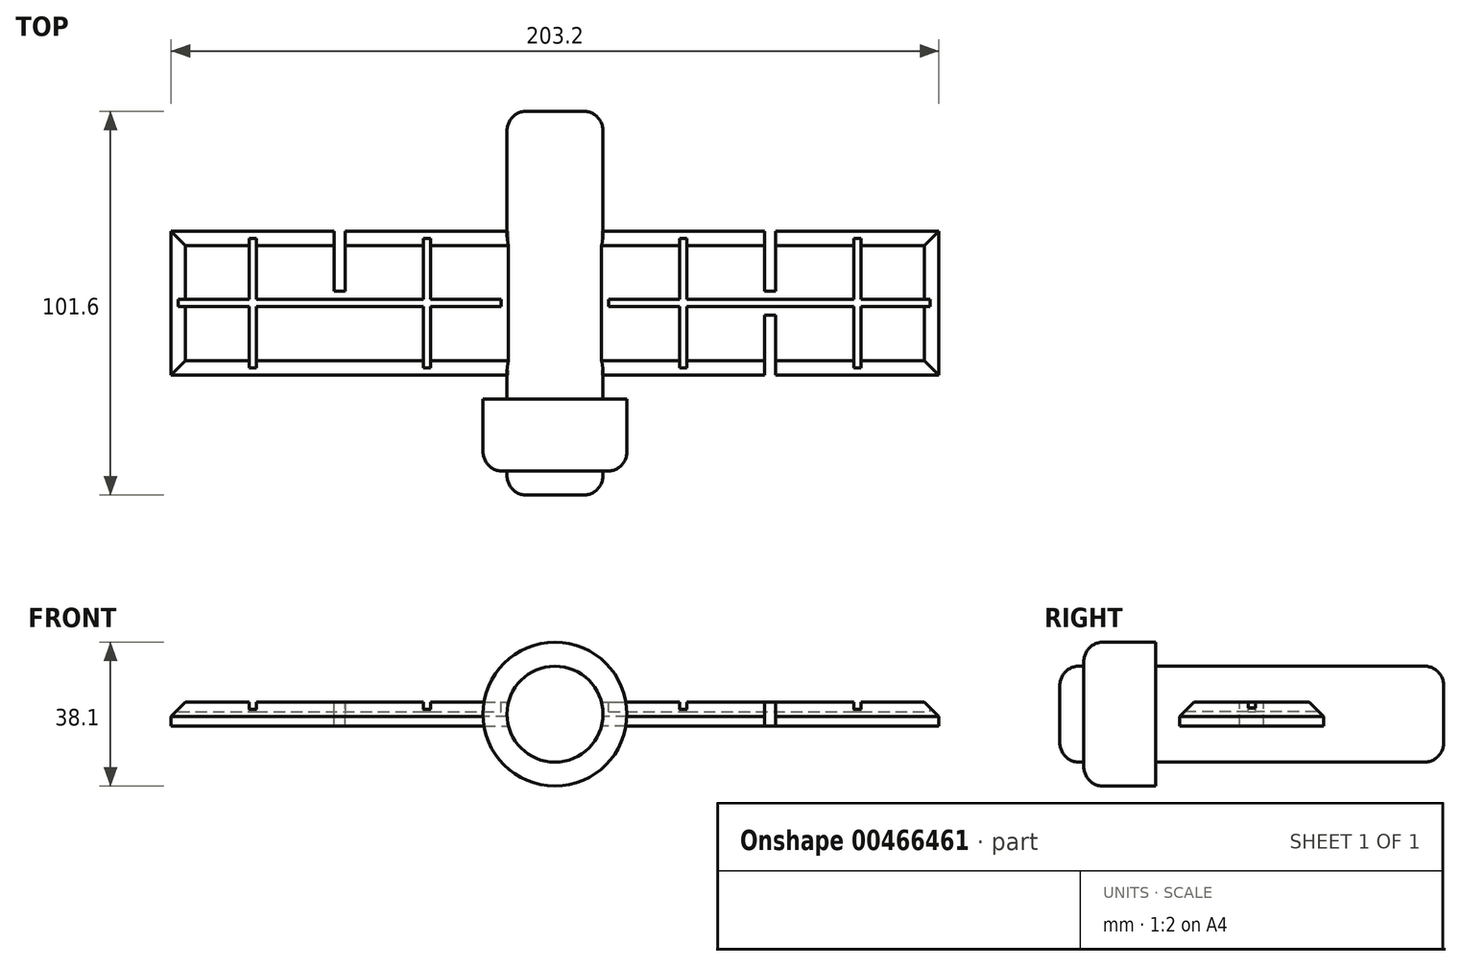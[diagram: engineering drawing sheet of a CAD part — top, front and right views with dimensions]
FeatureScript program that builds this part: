
annotation { "Feature Type Name" : "Feature", "Feature Type Description" : "" }
export const myFeature = defineFeature(function(context is Context, id is Id, definition is map)
    precondition{}
    {
        {
            var Q0;
            Q0=qCreatedBy(makeId("Front.planeOp"),FACE);
            cPlane(context, id + "F0", {"entities" : qUnion([Q0]), "cplaneType" : CPlaneType.OFFSET, "offset" : 50.8 * mm, "width" : 152.4 * mm, "height" : 152.4 * mm});
        }
        {
            var Q0;
            Q0=qCreatedBy(id+"F0.planeOp",FACE);
            var sketch = newSketch(context, id + "F1", { "sketchPlane" : qUnion([Q0])});
            skCircle(sketch, "E0", {"center": v(0, 0) * mm, "radius": 12.7 * mm});
            skSolve(sketch);
        }
        {
            var Q0;
            Q0=makeQuery(id+"F1.imprint","IMPRINT",FACE,{"disambiguationData":[TD([[makeQuery(id+"F1.imprint","IMPRINT",EDGE,{"derivedFrom":sQuery(id+"F1.wireOp",EDGE,"E0")}),1.0]])]});
            extrude(context, id + "F2", {"entities" : qUnion([Q0]), "oppositeDirection" : true, "depth" : 101.6 * mm});
        }
        {
            var Q0;
            Q0=makeQuery(id+"F2.opExtrude","CAP_EDGE",EDGE,{"disambiguationData":[OSD([sQuery(id+"F1.wireOp",EDGE,"E0")])],"isStart":true});
            var Q1;
            Q1=makeQuery(id+"F2.opExtrude","CAP_EDGE",EDGE,{"disambiguationData":[OSD([sQuery(id+"F1.wireOp",EDGE,"E0")])],"isStart":false});
            fillet(context, id + "F3", {"entities" : qUnion([Q0, Q1]), "radius" : 5.08 * mm, "tangentPropagation" : true, "allowEdgeOverflow" : false});
        }
        {
            var Q0;
            Q0=qCreatedBy(makeId("Right.planeOp"),FACE);
            var sketch = newSketch(context, id + "F4", { "sketchPlane" : qUnion([Q0])});
            skLineSegment(sketch, "E1.bottom", {"start": v(19.05, 3.17) * mm, "end": v(-19.05, 3.17) * mm});
            skLineSegment(sketch, "E1.top", {"start": v(19.05, -3.18) * mm, "end": v(-19.05, -3.18) * mm});
            skLineSegment(sketch, "E1.left", {"start": v(19.05, 3.17) * mm, "end": v(19.05, -3.18) * mm});
            skLineSegment(sketch, "E1.right", {"start": v(-19.05, 3.17) * mm, "end": v(-19.05, -3.18) * mm});
            skPoint(sketch, "E1.middle", {"position": v(0, 0) * mm});
            skSolve(sketch);
        }
        {
            var Q0;
            Q0 = qSketchRegion(id + "F4", true);
            extrude(context, id + "F5", {"entities" : qUnion([Q0]), "operationType" : NewBodyOperationType.ADD, "depth" : 101.6 * mm});
        }
        {
            var Q0;
            Q0 = qSketchRegion(id + "F4", true);
            extrude(context, id + "F6", {"entities" : qUnion([Q0]), "operationType" : NewBodyOperationType.ADD, "oppositeDirection" : true, "depth" : 101.6 * mm});
        }
        {
            var Q0;
            Q0=makeQuery(id+"F6.opExtrude","SWEPT_FACE",FACE,{"disambiguationData":[OSD([sQuery(id+"F4.wireOp",EDGE,"E1.bottom")])]});
            var sketch = newSketch(context, id + "F7", { "sketchPlane" : qUnion([Q0])});
            skLineSegment(sketch, "E2.bottom", {"start": v(-101.6, 19.05) * mm, "end": v(-58.42, 19.05) * mm, "construction": true});
            skLineSegment(sketch, "E2.top", {"start": v(-101.6, -19.05) * mm, "end": v(-58.42, -19.05) * mm, "construction": true});
            skLineSegment(sketch, "E2.left", {"start": v(-101.6, 19.05) * mm, "end": v(-101.6, -19.05) * mm, "construction": true});
            skLineSegment(sketch, "E2.right", {"start": v(-58.42, 19.05) * mm, "end": v(-58.42, -19.05) * mm, "construction": true});
            skLineSegment(sketch, "E3.bottom", {"start": v(-12.3, -19.05) * mm, "end": v(-55.48, -19.05) * mm, "construction": true});
            skLineSegment(sketch, "E3.top", {"start": v(-12.3, 19.05) * mm, "end": v(-55.48, 19.05) * mm, "construction": true});
            skLineSegment(sketch, "E3.left", {"start": v(-12.3, -19.05) * mm, "end": v(-12.3, 19.05) * mm, "construction": true});
            skLineSegment(sketch, "E3.right", {"start": v(-55.48, -19.05) * mm, "end": v(-55.48, 19.05) * mm, "construction": true});
            skLineSegment(sketch, "E4", {"start": v(-58.42, 0) * mm, "end": v(-55.48, 0) * mm, "construction": true});
            skLineSegment(sketch, "E5.top", {"start": v(-58.42, 3.18) * mm, "end": v(-55.48, 3.18) * mm, "construction": true});
            skLineSegment(sketch, "E5.left", {"start": v(-58.42, 0) * mm, "end": v(-58.42, 3.18) * mm, "construction": true});
            skLineSegment(sketch, "E5.right", {"start": v(-55.48, 0) * mm, "end": v(-55.48, 3.18) * mm, "construction": true});
            skLineSegment(sketch, "E6.bottom", {"start": v(-58.42, 0) * mm, "end": v(-55.48, 0) * mm});
            skLineSegment(sketch, "E6.top", {"start": v(-58.42, -3.17) * mm, "end": v(-55.48, -3.17) * mm});
            skLineSegment(sketch, "E6.left", {"start": v(-58.42, 0) * mm, "end": v(-58.42, -3.17) * mm});
            skLineSegment(sketch, "E6.right", {"start": v(-55.48, 0) * mm, "end": v(-55.48, -3.17) * mm});
            skLineSegment(sketch, "E7.top", {"start": v(-58.42, -19.05) * mm, "end": v(-55.48, -19.05) * mm});
            skLineSegment(sketch, "E7.left", {"start": v(-58.42, -3.17) * mm, "end": v(-58.42, -19.05) * mm});
            skLineSegment(sketch, "E7.right", {"start": v(-55.48, -3.17) * mm, "end": v(-55.48, -19.05) * mm});
            skLineSegment(sketch, "E8.bottom", {"start": v(-58.42, 19.05) * mm, "end": v(-55.48, 19.05) * mm});
            skLineSegment(sketch, "E8.top", {"start": v(-58.42, 3.18) * mm, "end": v(-55.48, 3.18) * mm});
            skLineSegment(sketch, "E8.left", {"start": v(-58.42, 19.05) * mm, "end": v(-58.42, 3.18) * mm});
            skLineSegment(sketch, "E8.right", {"start": v(-55.48, 19.05) * mm, "end": v(-55.48, 3.18) * mm});
            skSolve(sketch);
        }
        {
            var Q0;
            Q0=makeQuery(id+"F7.imprint","IMPRINT",FACE,{"disambiguationData":[TD([[makeQuery(id+"F7.imprint","IMPRINT",EDGE,{"derivedFrom":sQuery(id+"F7.wireOp",EDGE,"E8.bottom")}),-1.0]])]});
            var Q1;
            Q1=makeQuery(id+"F7.imprint","IMPRINT",FACE,{"disambiguationData":[TD([[makeQuery(id+"F7.imprint","IMPRINT",EDGE,{"derivedFrom":sQuery(id+"F7.wireOp",EDGE,"E6.top")}),-1.0]])]});
            extrude(context, id + "F8", {"entities" : qUnion([Q0, Q1]), "operationType" : NewBodyOperationType.REMOVE, "oppositeDirection" : true, "depth" : 25.4 * mm});
        }
        {
            var Q0;
            Q0=makeQuery(id+"F5.opExtrude","SWEPT_FACE",FACE,{"disambiguationData":[OSD([sQuery(id+"F4.wireOp",EDGE,"E1.bottom")])]});
            var sketch = newSketch(context, id + "F9", { "sketchPlane" : qUnion([Q0])});
            skLineSegment(sketch, "E9.bottom", {"start": v(12.3, 19.05) * mm, "end": v(55.48, 19.05) * mm, "construction": true});
            skLineSegment(sketch, "E9.top", {"start": v(12.3, -19.05) * mm, "end": v(55.48, -19.05) * mm, "construction": true});
            skLineSegment(sketch, "E9.left", {"start": v(12.3, 19.05) * mm, "end": v(12.3, -19.05) * mm, "construction": true});
            skLineSegment(sketch, "E9.right", {"start": v(55.48, 19.05) * mm, "end": v(55.48, -19.05) * mm, "construction": true});
            skLineSegment(sketch, "E10.bottom", {"start": v(101.6, -19.05) * mm, "end": v(58.42, -19.05) * mm, "construction": true});
            skLineSegment(sketch, "E10.top", {"start": v(101.6, 19.05) * mm, "end": v(58.42, 19.05) * mm, "construction": true});
            skLineSegment(sketch, "E10.left", {"start": v(101.6, -19.05) * mm, "end": v(101.6, 19.05) * mm, "construction": true});
            skLineSegment(sketch, "E10.right", {"start": v(58.42, -19.05) * mm, "end": v(58.42, 19.05) * mm, "construction": true});
            skLineSegment(sketch, "E11", {"start": v(55.48, 0) * mm, "end": v(58.42, 0) * mm, "construction": true});
            skLineSegment(sketch, "E12.top", {"start": v(55.48, 3.18) * mm, "end": v(58.42, 3.18) * mm, "construction": true});
            skLineSegment(sketch, "E12.left", {"start": v(55.48, 0) * mm, "end": v(55.48, 3.18) * mm, "construction": true});
            skLineSegment(sketch, "E12.right", {"start": v(58.42, 0) * mm, "end": v(58.42, 3.18) * mm, "construction": true});
            skLineSegment(sketch, "E13.top", {"start": v(55.48, -3.17) * mm, "end": v(58.42, -3.17) * mm, "construction": true});
            skLineSegment(sketch, "E13.left", {"start": v(55.48, 0) * mm, "end": v(55.48, -3.17) * mm, "construction": true});
            skLineSegment(sketch, "E13.right", {"start": v(58.42, 0) * mm, "end": v(58.42, -3.17) * mm, "construction": true});
            skLineSegment(sketch, "E14.bottom", {"start": v(55.48, -3.17) * mm, "end": v(58.42, -3.17) * mm});
            skLineSegment(sketch, "E14.top", {"start": v(55.48, -19.05) * mm, "end": v(58.42, -19.05) * mm});
            skLineSegment(sketch, "E14.left", {"start": v(55.48, -3.17) * mm, "end": v(55.48, -19.05) * mm});
            skLineSegment(sketch, "E14.right", {"start": v(58.42, -3.17) * mm, "end": v(58.42, -19.05) * mm});
            skLineSegment(sketch, "E15.bottom", {"start": v(55.48, 19.05) * mm, "end": v(58.42, 19.05) * mm});
            skLineSegment(sketch, "E15.top", {"start": v(55.48, 3.18) * mm, "end": v(58.42, 3.18) * mm});
            skLineSegment(sketch, "E15.left", {"start": v(55.48, 19.05) * mm, "end": v(55.48, 3.18) * mm});
            skLineSegment(sketch, "E15.right", {"start": v(58.42, 19.05) * mm, "end": v(58.42, 3.18) * mm});
            skSolve(sketch);
        }
        {
            var Q0;
            Q0=makeQuery(id+"F9.imprint","IMPRINT",FACE,{"disambiguationData":[TD([[makeQuery(id+"F9.imprint","IMPRINT",EDGE,{"derivedFrom":sQuery(id+"F9.wireOp",EDGE,"E15.bottom")}),1.0]])]});
            var Q1;
            Q1=makeQuery(id+"F9.imprint","IMPRINT",FACE,{"disambiguationData":[TD([[makeQuery(id+"F9.imprint","IMPRINT",EDGE,{"derivedFrom":sQuery(id+"F9.wireOp",EDGE,"E14.bottom")}),-1.0]])]});
            extrude(context, id + "F10", {"entities" : qUnion([Q0, Q1]), "operationType" : NewBodyOperationType.REMOVE, "oppositeDirection" : true, "depth" : 25.4 * mm});
        }
        {
            var Q0;
            Q0=makeQuery(id+"F6.opExtrude","SWEPT_FACE",FACE,{"disambiguationData":[OSD([sQuery(id+"F4.wireOp",EDGE,"E1.bottom")])]});
            var sketch = newSketch(context, id + "F11", { "sketchPlane" : qUnion([Q0])});
            skLineSegment(sketch, "E16.bottom", {"start": v(-79.06, 19.05) * mm, "end": v(-80.96, 19.05) * mm, "construction": true});
            skLineSegment(sketch, "E16.top", {"start": v(-79.06, 19.05) * mm, "end": v(-80.96, 19.05) * mm, "construction": true});
            skLineSegment(sketch, "E16.left", {"start": v(-79.06, 19.05) * mm, "end": v(-79.06, 19.05) * mm});
            skLineSegment(sketch, "E16.right", {"start": v(-80.96, 19.05) * mm, "end": v(-80.96, 19.05) * mm});
            skPoint(sketch, "E16.middle", {"position": v(-80.01, 19.05) * mm});
            skLineSegment(sketch, "E17", {"start": v(-80.96, 19.05) * mm, "end": v(-80.96, 17.15) * mm, "construction": true});
            skLineSegment(sketch, "E18.bottom", {"start": v(-80.96, 17.15) * mm, "end": v(-79.06, 17.15) * mm});
            skLineSegment(sketch, "E18.top", {"start": v(-80.96, -17.14) * mm, "end": v(-79.06, -17.14) * mm});
            skLineSegment(sketch, "E18.left", {"start": v(-80.96, 17.15) * mm, "end": v(-80.96, -17.14) * mm});
            skLineSegment(sketch, "E18.right", {"start": v(-79.06, 17.15) * mm, "end": v(-79.06, -17.14) * mm});
            skLineSegment(sketch, "E19.bottom", {"start": v(-101.6, 0.95) * mm, "end": v(-101.6, 0.95) * mm});
            skLineSegment(sketch, "E19.top", {"start": v(-101.6, -0.95) * mm, "end": v(-101.6, -0.95) * mm});
            skLineSegment(sketch, "E19.left", {"start": v(-101.6, 0.95) * mm, "end": v(-101.6, -0.95) * mm, "construction": true});
            skLineSegment(sketch, "E19.right", {"start": v(-101.6, 0.95) * mm, "end": v(-101.6, -0.95) * mm, "construction": true});
            skPoint(sketch, "E19.middle", {"position": v(-101.6, 0) * mm});
            skLineSegment(sketch, "E20.bottom", {"start": v(-101.6, -0.95) * mm, "end": v(-99.7, -0.95) * mm, "construction": true});
            skLineSegment(sketch, "E20.top", {"start": v(-101.6, 0.95) * mm, "end": v(-99.7, 0.95) * mm, "construction": true});
            skLineSegment(sketch, "E20.left", {"start": v(-101.6, -0.95) * mm, "end": v(-101.6, 0.95) * mm, "construction": true});
            skLineSegment(sketch, "E20.right", {"start": v(-99.7, -0.95) * mm, "end": v(-99.7, 0.95) * mm, "construction": true});
            skLineSegment(sketch, "E21.bottom", {"start": v(-99.7, -0.95) * mm, "end": v(-14.2, -0.95) * mm});
            skLineSegment(sketch, "E21.top", {"start": v(-99.7, 0.95) * mm, "end": v(-14.2, 0.95) * mm});
            skLineSegment(sketch, "E21.left", {"start": v(-99.7, -0.95) * mm, "end": v(-99.7, 0.95) * mm});
            skLineSegment(sketch, "E21.right", {"start": v(-14.2, -0.95) * mm, "end": v(-14.2, 0.95) * mm});
            skLineSegment(sketch, "E22", {"start": v(-14.2, 0.95) * mm, "end": v(-12.3, 0.95) * mm, "construction": true});
            skLineSegment(sketch, "E23.bottom", {"start": v(-32.93, 19.05) * mm, "end": v(-34.84, 19.05) * mm});
            skLineSegment(sketch, "E23.top", {"start": v(-32.93, 19.05) * mm, "end": v(-34.84, 19.05) * mm, "construction": true});
            skLineSegment(sketch, "E23.left", {"start": v(-32.93, 19.05) * mm, "end": v(-32.93, 19.05) * mm});
            skLineSegment(sketch, "E23.right", {"start": v(-34.84, 19.05) * mm, "end": v(-34.84, 19.05) * mm});
            skPoint(sketch, "E23.middle", {"position": v(-33.89, 19.05) * mm});
            skLineSegment(sketch, "E24.bottom", {"start": v(-34.84, 19.05) * mm, "end": v(-32.95, 19.05) * mm, "construction": true});
            skLineSegment(sketch, "E24.top", {"start": v(-34.84, 17.15) * mm, "end": v(-32.95, 17.15) * mm, "construction": true});
            skLineSegment(sketch, "E24.left", {"start": v(-34.84, 19.05) * mm, "end": v(-34.84, 17.15) * mm, "construction": true});
            skLineSegment(sketch, "E24.right", {"start": v(-32.95, 19.05) * mm, "end": v(-32.95, 17.15) * mm, "construction": true});
            skLineSegment(sketch, "E25.bottom", {"start": v(-34.84, 17.15) * mm, "end": v(-32.94, 17.15) * mm});
            skLineSegment(sketch, "E25.top", {"start": v(-34.84, -17.15) * mm, "end": v(-32.94, -17.15) * mm});
            skLineSegment(sketch, "E25.left", {"start": v(-34.84, 17.15) * mm, "end": v(-34.84, -17.14) * mm});
            skLineSegment(sketch, "E25.right", {"start": v(-32.94, 17.15) * mm, "end": v(-32.94, -17.15) * mm});
            skSolve(sketch);
        }
        {
            var Q0;
            {var subQ0=sQuery(id+"F11.wireOp",EDGE,"E18.bottom");Q0=makeQuery(id+"F11.imprint","IMPRINT",FACE,{"disambiguationData":[TD([[makeQuery(id+"F11.imprint","IMPRINT",EDGE,{"derivedFrom":subQ0}),-1.0]])]});}
            var Q1;
            {var subQ5=sQuery(id+"F11.wireOp",EDGE,"E21.left");Q1=makeQuery(id+"F11.imprint","IMPRINT",FACE,{"disambiguationData":[TD([[makeQuery(id+"F11.imprint","IMPRINT",EDGE,{"derivedFrom":subQ5}),-1.0]])]});}
            var Q2;
            {var subQ0=sQuery(id+"F11.wireOp",EDGE,"E21.top");var subQ1=sQuery(id+"F11.wireOp",EDGE,"E18.left");var subQ2=makeQuery(id+"F11.imprint","INTERSECT",VERTEX,{"derivedFrom":[subQ1,subQ0]});Q2=makeQuery(id+"F11.imprint","IMPRINT",FACE,{"disambiguationData":[TD([[makeQuery(id+"F11.imprint","IMPRINT",EDGE,{"disambiguationData":[TD([[subQ2,-1.0]])],"derivedFrom":subQ1}),1.0]])]});}
            var Q3;
            {var subQ0=sQuery(id+"F11.wireOp",EDGE,"E18.top");Q3=makeQuery(id+"F11.imprint","IMPRINT",FACE,{"disambiguationData":[TD([[makeQuery(id+"F11.imprint","IMPRINT",EDGE,{"derivedFrom":subQ0}),1.0]])]});}
            var Q4;
            {var subQ0=sQuery(id+"F11.wireOp",EDGE,"E21.top");var subQ1=sQuery(id+"F11.wireOp",EDGE,"E18.right");var subQ2=makeQuery(id+"F11.imprint","INTERSECT",VERTEX,{"derivedFrom":[subQ1,subQ0]});Q4=makeQuery(id+"F11.imprint","IMPRINT",FACE,{"disambiguationData":[TD([[makeQuery(id+"F11.imprint","IMPRINT",EDGE,{"disambiguationData":[TD([[subQ2,-1.0]])],"derivedFrom":subQ1}),1.0]])]});}
            var Q5;
            {var subQ5=sQuery(id+"F11.wireOp",EDGE,"E25.top");Q5=makeQuery(id+"F11.imprint","IMPRINT",FACE,{"disambiguationData":[TD([[makeQuery(id+"F11.imprint","IMPRINT",EDGE,{"derivedFrom":subQ5}),1.0]])]});}
            var Q6;
            {var subQ0=sQuery(id+"F11.wireOp",EDGE,"E25.left");var subQ1=sQuery(id+"F11.wireOp",EDGE,"E21.bottom");var subQ2=makeQuery(id+"F11.imprint","INTERSECT",VERTEX,{"derivedFrom":[subQ1,subQ0]});Q6=makeQuery(id+"F11.imprint","IMPRINT",FACE,{"disambiguationData":[TD([[makeQuery(id+"F11.imprint","IMPRINT",EDGE,{"disambiguationData":[TD([[subQ2,-1.0]])],"derivedFrom":subQ1}),1.0]])]});}
            var Q7;
            {var subQ5=sQuery(id+"F11.wireOp",EDGE,"E25.bottom");Q7=makeQuery(id+"F11.imprint","IMPRINT",FACE,{"disambiguationData":[TD([[makeQuery(id+"F11.imprint","IMPRINT",EDGE,{"derivedFrom":subQ5}),-1.0]])]});}
            var Q8;
            {var subQ0=sQuery(id+"F11.wireOp",EDGE,"E21.right");Q8=makeQuery(id+"F11.imprint","IMPRINT",FACE,{"disambiguationData":[TD([[makeQuery(id+"F11.imprint","IMPRINT",EDGE,{"derivedFrom":subQ0}),1.0]])]});}
            extrude(context, id + "F12", {"entities" : qUnion([Q0, Q1, Q2, Q3, Q4, Q5, Q6, Q7, Q8]), "operationType" : NewBodyOperationType.REMOVE, "oppositeDirection" : true, "depth" : 2.54 * mm});
        }
        {
            var Q0;
            Q0=makeQuery(id+"F5.opExtrude","SWEPT_FACE",FACE,{"disambiguationData":[OSD([sQuery(id+"F4.wireOp",EDGE,"E1.bottom")])]});
            var sketch = newSketch(context, id + "F13", { "sketchPlane" : qUnion([Q0])});
            skLineSegment(sketch, "E26.bottom", {"start": v(34.84, 19.05) * mm, "end": v(32.93, 19.05) * mm});
            skLineSegment(sketch, "E26.top", {"start": v(34.84, 19.05) * mm, "end": v(32.93, 19.05) * mm, "construction": true});
            skLineSegment(sketch, "E26.left", {"start": v(34.84, 19.05) * mm, "end": v(34.84, 19.05) * mm});
            skLineSegment(sketch, "E26.right", {"start": v(32.93, 19.05) * mm, "end": v(32.93, 19.05) * mm});
            skPoint(sketch, "E26.middle", {"position": v(33.89, 19.05) * mm});
            skLineSegment(sketch, "E27.bottom", {"start": v(32.93, 19.05) * mm, "end": v(34.84, 19.05) * mm});
            skLineSegment(sketch, "E27.top", {"start": v(32.93, 17.15) * mm, "end": v(34.84, 17.15) * mm, "construction": true});
            skLineSegment(sketch, "E27.left", {"start": v(32.93, 19.05) * mm, "end": v(32.93, 17.15) * mm, "construction": true});
            skLineSegment(sketch, "E27.right", {"start": v(34.84, 19.05) * mm, "end": v(34.84, 17.15) * mm, "construction": true});
            skLineSegment(sketch, "E28.bottom", {"start": v(32.93, 17.15) * mm, "end": v(34.85, 17.15) * mm});
            skLineSegment(sketch, "E28.top", {"start": v(32.93, -17.15) * mm, "end": v(34.85, -17.15) * mm});
            skLineSegment(sketch, "E28.left", {"start": v(32.93, 17.15) * mm, "end": v(32.93, -17.15) * mm});
            skLineSegment(sketch, "E28.right", {"start": v(34.85, 17.15) * mm, "end": v(34.85, -17.15) * mm});
            skLineSegment(sketch, "E29.bottom", {"start": v(80.96, 19.05) * mm, "end": v(79.06, 19.05) * mm, "construction": true});
            skLineSegment(sketch, "E29.top", {"start": v(80.96, 19.05) * mm, "end": v(79.06, 19.05) * mm, "construction": true});
            skLineSegment(sketch, "E29.left", {"start": v(80.96, 19.05) * mm, "end": v(80.96, 19.05) * mm});
            skLineSegment(sketch, "E29.right", {"start": v(79.06, 19.05) * mm, "end": v(79.06, 19.05) * mm});
            skPoint(sketch, "E29.middle", {"position": v(80.01, 19.05) * mm});
            skLineSegment(sketch, "E30.bottom", {"start": v(79.06, 19.05) * mm, "end": v(80.96, 19.05) * mm, "construction": true});
            skLineSegment(sketch, "E30.top", {"start": v(79.06, 17.15) * mm, "end": v(80.96, 17.15) * mm, "construction": true});
            skLineSegment(sketch, "E30.left", {"start": v(79.06, 19.05) * mm, "end": v(79.06, 17.15) * mm, "construction": true});
            skLineSegment(sketch, "E30.right", {"start": v(80.96, 19.05) * mm, "end": v(80.96, 17.15) * mm, "construction": true});
            skLineSegment(sketch, "E31.bottom", {"start": v(79.06, 17.15) * mm, "end": v(80.96, 17.15) * mm});
            skLineSegment(sketch, "E31.top", {"start": v(79.06, -17.14) * mm, "end": v(80.96, -17.14) * mm});
            skLineSegment(sketch, "E31.left", {"start": v(79.06, 17.15) * mm, "end": v(79.06, -17.14) * mm});
            skLineSegment(sketch, "E31.right", {"start": v(80.96, 17.15) * mm, "end": v(80.96, -17.14) * mm});
            skLineSegment(sketch, "E32.bottom", {"start": v(12.3, 0.95) * mm, "end": v(12.3, 0.95) * mm});
            skLineSegment(sketch, "E32.top", {"start": v(12.3, -0.95) * mm, "end": v(12.3, -0.95) * mm});
            skLineSegment(sketch, "E32.left", {"start": v(12.3, 0.95) * mm, "end": v(12.3, -0.95) * mm, "construction": true});
            skLineSegment(sketch, "E32.right", {"start": v(12.3, 0.95) * mm, "end": v(12.3, -0.95) * mm, "construction": true});
            skPoint(sketch, "E32.middle", {"position": v(12.3, 0) * mm});
            skLineSegment(sketch, "E33.bottom", {"start": v(12.3, -0.95) * mm, "end": v(14.2, -0.95) * mm, "construction": true});
            skLineSegment(sketch, "E33.top", {"start": v(12.3, 0.95) * mm, "end": v(14.2, 0.95) * mm, "construction": true});
            skLineSegment(sketch, "E33.left", {"start": v(12.3, -0.95) * mm, "end": v(12.3, 0.95) * mm, "construction": true});
            skLineSegment(sketch, "E33.right", {"start": v(14.2, -0.95) * mm, "end": v(14.2, 0.95) * mm, "construction": true});
            skLineSegment(sketch, "E34.bottom", {"start": v(14.2, -0.95) * mm, "end": v(99.3, -0.95) * mm});
            skLineSegment(sketch, "E34.top", {"start": v(14.2, 0.95) * mm, "end": v(99.3, 0.95) * mm});
            skLineSegment(sketch, "E34.left", {"start": v(14.2, -0.95) * mm, "end": v(14.2, 0.95) * mm});
            skLineSegment(sketch, "E34.right", {"start": v(99.3, -0.95) * mm, "end": v(99.3, 0.95) * mm});
            skSolve(sketch);
        }
        {
            var Q0;
            {var subQ5=sQuery(id+"F13.wireOp",EDGE,"E34.left");Q0=makeQuery(id+"F13.imprint","IMPRINT",FACE,{"disambiguationData":[TD([[makeQuery(id+"F13.imprint","IMPRINT",EDGE,{"derivedFrom":subQ5}),-1.0]])]});}
            var Q1;
            {var subQ0=sQuery(id+"F13.wireOp",EDGE,"E28.bottom");Q1=makeQuery(id+"F13.imprint","IMPRINT",FACE,{"disambiguationData":[TD([[makeQuery(id+"F13.imprint","IMPRINT",EDGE,{"derivedFrom":subQ0}),-1.0]])]});}
            var Q2;
            {var subQ0=sQuery(id+"F13.wireOp",EDGE,"E34.top");var subQ1=sQuery(id+"F13.wireOp",EDGE,"E28.left");var subQ2=makeQuery(id+"F13.imprint","INTERSECT",VERTEX,{"derivedFrom":[subQ1,subQ0]});Q2=makeQuery(id+"F13.imprint","IMPRINT",FACE,{"disambiguationData":[TD([[makeQuery(id+"F13.imprint","IMPRINT",EDGE,{"disambiguationData":[TD([[subQ2,-1.0]])],"derivedFrom":subQ1}),1.0]])]});}
            var Q3;
            {var subQ0=sQuery(id+"F13.wireOp",EDGE,"E28.top");Q3=makeQuery(id+"F13.imprint","IMPRINT",FACE,{"disambiguationData":[TD([[makeQuery(id+"F13.imprint","IMPRINT",EDGE,{"derivedFrom":subQ0}),1.0]])]});}
            var Q4;
            {var subQ0=sQuery(id+"F13.wireOp",EDGE,"E34.top");var subQ1=sQuery(id+"F13.wireOp",EDGE,"E28.right");var subQ2=makeQuery(id+"F13.imprint","INTERSECT",VERTEX,{"derivedFrom":[subQ1,subQ0]});Q4=makeQuery(id+"F13.imprint","IMPRINT",FACE,{"disambiguationData":[TD([[makeQuery(id+"F13.imprint","IMPRINT",EDGE,{"disambiguationData":[TD([[subQ2,-1.0]])],"derivedFrom":subQ1}),1.0]])]});}
            var Q5;
            {var subQ0=sQuery(id+"F13.wireOp",EDGE,"E31.bottom");Q5=makeQuery(id+"F13.imprint","IMPRINT",FACE,{"disambiguationData":[TD([[makeQuery(id+"F13.imprint","IMPRINT",EDGE,{"derivedFrom":subQ0}),-1.0]])]});}
            var Q6;
            {var subQ0=sQuery(id+"F13.wireOp",EDGE,"E34.top");var subQ1=sQuery(id+"F13.wireOp",EDGE,"E31.left");var subQ2=makeQuery(id+"F13.imprint","INTERSECT",VERTEX,{"derivedFrom":[subQ1,subQ0]});Q6=makeQuery(id+"F13.imprint","IMPRINT",FACE,{"disambiguationData":[TD([[makeQuery(id+"F13.imprint","IMPRINT",EDGE,{"disambiguationData":[TD([[subQ2,-1.0]])],"derivedFrom":subQ1}),1.0]])]});}
            var Q7;
            {var subQ5=sQuery(id+"F13.wireOp",EDGE,"E34.right");Q7=makeQuery(id+"F13.imprint","IMPRINT",FACE,{"disambiguationData":[TD([[makeQuery(id+"F13.imprint","IMPRINT",EDGE,{"derivedFrom":subQ5}),1.0]])]});}
            var Q8;
            {var subQ0=sQuery(id+"F13.wireOp",EDGE,"E31.top");Q8=makeQuery(id+"F13.imprint","IMPRINT",FACE,{"disambiguationData":[TD([[makeQuery(id+"F13.imprint","IMPRINT",EDGE,{"derivedFrom":subQ0}),1.0]])]});}
            extrude(context, id + "F14", {"entities" : qUnion([Q0, Q1, Q2, Q3, Q4, Q5, Q6, Q7, Q8]), "operationType" : NewBodyOperationType.REMOVE, "oppositeDirection" : true, "depth" : 2.54 * mm});
        }
        {
            var Q0;
            Q0=makeQuery(id+"F6.opExtrude","CAP_EDGE",EDGE,{"disambiguationData":[OSD([sQuery(id+"F4.wireOp",EDGE,"E1.bottom")])],"isStart":false});
            var Q1;
            Q1=makeQuery(id+"F5.opExtrude","CAP_EDGE",EDGE,{"disambiguationData":[OSD([sQuery(id+"F4.wireOp",EDGE,"E1.bottom")])],"isStart":false});
            var Q2;
            {var subQ0=sQuery(id+"F4.wireOp",EDGE,"E1.bottom");var subQ1=sQuery(id+"F4.wireOp",EDGE,"E1.left");Q2=makeQuery(id+"F10.boolean.opBoolean","SPLIT",EDGE,{"disambiguationData":[TD([makeQuery(id+"F10.opExtrude","SWEPT_FACE",FACE,{"disambiguationData":[OSD([sQuery(id+"F9.wireOp",EDGE,"E15.right")])]})])],"derivedFrom":makeQuery(id+"F5.opExtrude","SWEPT_EDGE",EDGE,{"disambiguationData":[OSD([subQ0,subQ1])]})});}
            var Q3;
            {var subQ0=sQuery(id+"F4.wireOp",EDGE,"E1.bottom");var subQ1=sQuery(id+"F4.wireOp",EDGE,"E1.left");Q3=makeQuery(id+"F10.boolean.opBoolean","SPLIT",EDGE,{"disambiguationData":[TD([makeQuery(id+"F2.opExtrude","SWEPT_FACE",FACE,{"disambiguationData":[OSD([sQuery(id+"F1.wireOp",EDGE,"E0")])]})])],"derivedFrom":makeQuery(id+"F5.opExtrude","SWEPT_EDGE",EDGE,{"disambiguationData":[OSD([subQ0,subQ1])]})});}
            var Q4;
            {var subQ0=sQuery(id+"F4.wireOp",EDGE,"E1.bottom");var subQ1=sQuery(id+"F4.wireOp",EDGE,"E1.right");Q4=makeQuery(id+"F10.boolean.opBoolean","SPLIT",EDGE,{"disambiguationData":[TD([makeQuery(id+"F2.opExtrude","SWEPT_FACE",FACE,{"disambiguationData":[OSD([sQuery(id+"F1.wireOp",EDGE,"E0")])]})])],"derivedFrom":makeQuery(id+"F5.opExtrude","SWEPT_EDGE",EDGE,{"disambiguationData":[OSD([subQ0,subQ1])]})});}
            var Q5;
            {var subQ0=sQuery(id+"F4.wireOp",EDGE,"E1.bottom");var subQ1=sQuery(id+"F4.wireOp",EDGE,"E1.right");Q5=makeQuery(id+"F10.boolean.opBoolean","SPLIT",EDGE,{"disambiguationData":[TD([makeQuery(id+"F10.opExtrude","SWEPT_FACE",FACE,{"disambiguationData":[OSD([sQuery(id+"F9.wireOp",EDGE,"E14.right")])]})])],"derivedFrom":makeQuery(id+"F5.opExtrude","SWEPT_EDGE",EDGE,{"disambiguationData":[OSD([subQ0,subQ1])]})});}
            var Q6;
            {var subQ0=sQuery(id+"F4.wireOp",EDGE,"E1.bottom");var subQ1=sQuery(id+"F4.wireOp",EDGE,"E1.right");Q6=makeQuery(id+"F8.boolean.opBoolean","SPLIT",EDGE,{"disambiguationData":[TD([makeQuery(id+"F2.opExtrude","SWEPT_FACE",FACE,{"disambiguationData":[OSD([sQuery(id+"F1.wireOp",EDGE,"E0")])]})])],"derivedFrom":makeQuery(id+"F6.opExtrude","SWEPT_EDGE",EDGE,{"disambiguationData":[OSD([subQ0,subQ1])]})});}
            var Q7;
            {var subQ0=sQuery(id+"F4.wireOp",EDGE,"E1.bottom");var subQ1=sQuery(id+"F4.wireOp",EDGE,"E1.right");Q7=makeQuery(id+"F8.boolean.opBoolean","SPLIT",EDGE,{"disambiguationData":[TD([makeQuery(id+"F8.opExtrude","SWEPT_FACE",FACE,{"disambiguationData":[OSD([sQuery(id+"F7.wireOp",EDGE,"E7.left")])]})])],"derivedFrom":makeQuery(id+"F6.opExtrude","SWEPT_EDGE",EDGE,{"disambiguationData":[OSD([subQ0,subQ1])]})});}
            var Q8;
            {var subQ0=sQuery(id+"F4.wireOp",EDGE,"E1.bottom");var subQ1=sQuery(id+"F4.wireOp",EDGE,"E1.left");Q8=makeQuery(id+"F8.boolean.opBoolean","SPLIT",EDGE,{"disambiguationData":[TD([makeQuery(id+"F8.opExtrude","SWEPT_FACE",FACE,{"disambiguationData":[OSD([sQuery(id+"F7.wireOp",EDGE,"E8.left")])]})])],"derivedFrom":makeQuery(id+"F6.opExtrude","SWEPT_EDGE",EDGE,{"disambiguationData":[OSD([subQ0,subQ1])]})});}
            var Q9;
            {var subQ0=sQuery(id+"F4.wireOp",EDGE,"E1.left");var subQ1=sQuery(id+"F4.wireOp",EDGE,"E1.bottom");Q9=makeQuery(id+"F8.boolean.opBoolean","SPLIT",EDGE,{"disambiguationData":[TD([makeQuery(id+"F2.opExtrude","SWEPT_FACE",FACE,{"disambiguationData":[OSD([sQuery(id+"F1.wireOp",EDGE,"E0")])]})])],"derivedFrom":makeQuery(id+"F6.opExtrude","SWEPT_EDGE",EDGE,{"disambiguationData":[OSD([subQ1,subQ0])]})});}
            chamfer(context, id + "F15", {"entities" : qUnion([Q0, Q1, Q2, Q3, Q4, Q5, Q6, Q7, Q8, Q9]), "width" : 3.8 * mm, "tangentPropagation" : true});
        }
        {
            var Q0;
            Q0=qCreatedBy(makeId("Front.planeOp"),FACE);
            cPlane(context, id + "F16", {"entities" : qUnion([Q0]), "cplaneType" : CPlaneType.OFFSET, "offset" : 25.4 * mm, "width" : 152.4 * mm, "height" : 152.4 * mm});
        }
        {
            var Q0;
            Q0=qCreatedBy(id+"F16.planeOp",FACE);
            var sketch = newSketch(context, id + "F17", { "sketchPlane" : qUnion([Q0])});
            skCircle(sketch, "E35", {"center": v(0, 0) * mm, "radius": 19.05 * mm});
            skSolve(sketch);
        }
        {
            var Q0;
            Q0=makeQuery(id+"F17.imprint","IMPRINT",FACE,{"disambiguationData":[TD([[makeQuery(id+"F17.imprint","IMPRINT",EDGE,{"derivedFrom":sQuery(id+"F17.wireOp",EDGE,"E35")}),1.0]])]});
            extrude(context, id + "F18", {"entities" : qUnion([Q0]), "operationType" : NewBodyOperationType.ADD, "depth" : 19.05 * mm});
        }
        {
            var Q0;
            Q0=makeQuery(id+"F18.opExtrude","CAP_EDGE",EDGE,{"disambiguationData":[OSD([sQuery(id+"F17.wireOp",EDGE,"E35")])],"isStart":false});
            var Q1;
            {var subQ0=sQuery(id+"F1.wireOp",EDGE,"E0");Q1=makeQuery(id+"F3.opFillet","BLEND_EDGE",EDGE,{"blendedFrom":[makeQuery(id+"F2.opExtrude","CAP_EDGE",EDGE,{"disambiguationData":[OSD([subQ0])],"isStart":true}),makeQuery(id+"F2.opExtrude","CAP_FACE",FACE,{"disambiguationData":[OSD([subQ0])],"isStart":true})],"blendedInto":[makeQuery(id+"F2.opExtrude","CAP_FACE",FACE,{"disambiguationData":[OSD([subQ0])],"isStart":true})]});}
            fillet(context, id + "F19", {"entities" : qUnion([Q0, Q1]), "radius" : 5.08 * mm, "tangentPropagation" : true, "allowEdgeOverflow" : false});
        }
    });
